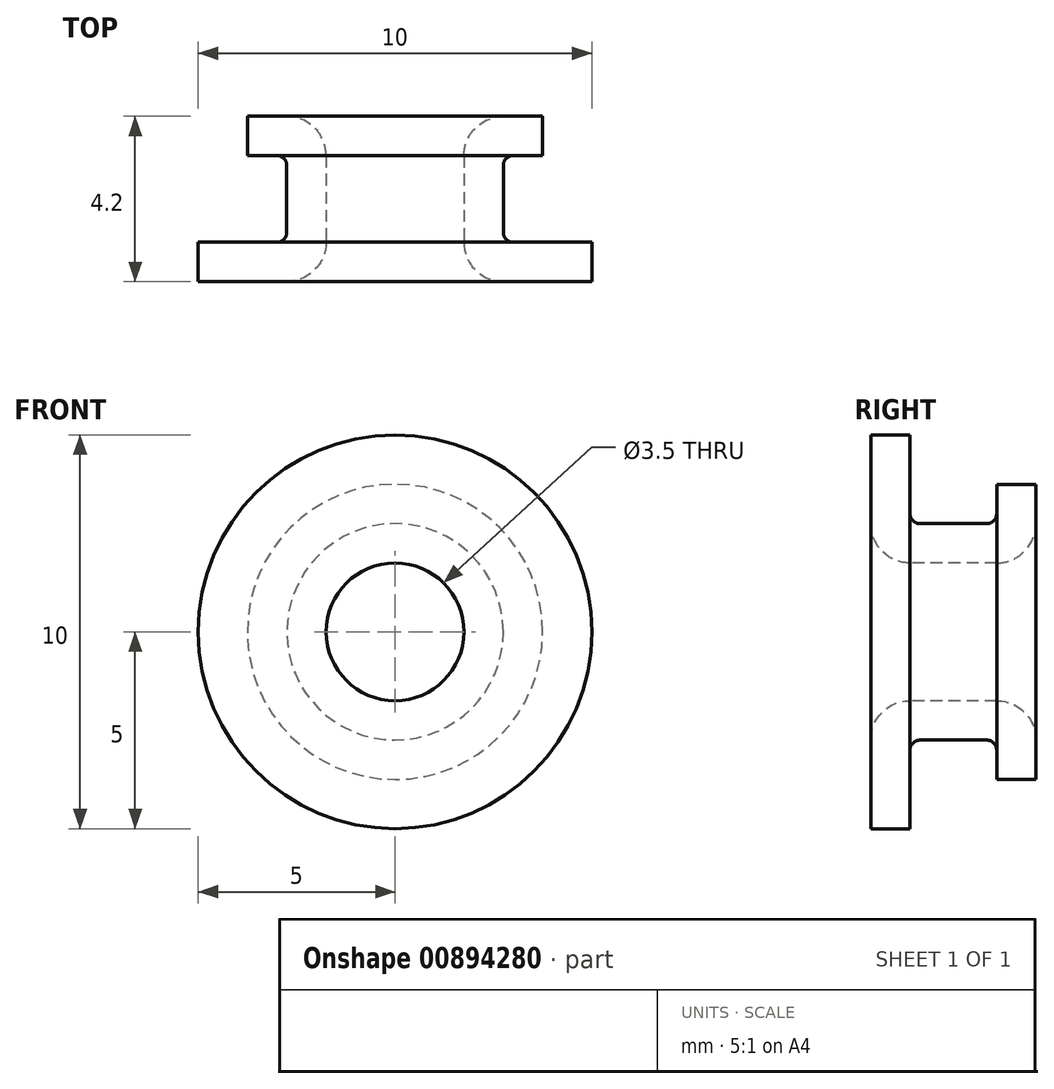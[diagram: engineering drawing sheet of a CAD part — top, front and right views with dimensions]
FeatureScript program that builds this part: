
annotation { "Feature Type Name" : "Feature", "Feature Type Description" : "" }
export const myFeature = defineFeature(function(context is Context, id is Id, definition is map)
    precondition{}
    {
        {
            var Q0;
            Q0=qCreatedBy(makeId("Right.planeOp"),FACE);
            var sketch = newSketch(context, id + "F0", { "sketchPlane" : qUnion([Q0])});
            skLineSegment(sketch, "E0", {"start": v(1, 5) * mm, "end": v(1, 3) * mm});
            skLineSegment(sketch, "E1", {"start": v(1.25, 2.75) * mm, "end": v(2.95, 2.75) * mm});
            skLineSegment(sketch, "E2", {"start": v(1, 1.75) * mm, "end": v(3.2, 1.75) * mm});
            skLineSegment(sketch, "E3", {"start": v(0, 0) * mm, "end": v(4.2, 0) * mm});
            skPoint(sketch, "E4.visualSharp", {"position": v(1, 2.75) * mm});
            skArc(sketch, "E4.filletArc", {"start": v(1, 3) * mm, "mid": v(1.07, 2.82) * mm, "end": v(1.25, 2.75) * mm});
            skPoint(sketch, "E5.visualSharp", {"position": v(3.2, 2.75) * mm});
            skLineSegment(sketch, "E6", {"start": v(4.2, 3.75) * mm, "end": v(4.2, 2.75) * mm});
            skArc(sketch, "E7", {"start": v(0, 2.75) * mm, "mid": v(0.3, 2.04) * mm, "end": v(1, 1.75) * mm});
            skLineSegment(sketch, "E8", {"start": v(0, 2.75) * mm, "end": v(0, 5) * mm});
            skLineSegment(sketch, "E9", {"start": v(1, 5) * mm, "end": v(0, 5) * mm});
            skLineSegment(sketch, "E10", {"start": v(4.2, 3.75) * mm, "end": v(3.2, 3.75) * mm});
            skLineSegment(sketch, "E11", {"start": v(3.2, 3.75) * mm, "end": v(3.2, 3) * mm});
            skArc(sketch, "E12.filletArc", {"start": v(2.95, 2.75) * mm, "mid": v(3.13, 2.82) * mm, "end": v(3.2, 3) * mm});
            skArc(sketch, "E13.filletArc", {"start": v(3.2, 1.75) * mm, "mid": v(3.9, 2.04) * mm, "end": v(4.2, 2.75) * mm});
            skSolve(sketch);
        }
        {
            var Q0;
            Q0=makeQuery(id+"F0.imprint","IMPRINT",FACE,{"disambiguationData":[TD([[makeQuery(id+"F0.imprint","IMPRINT",EDGE,{"derivedFrom":sQuery(id+"F0.wireOp",EDGE,"E0")}),-1.0]])]});
            var Q1;
            Q1=sQuery(id+"F0.wireOp",EDGE,"E3");
            revolve(context, id + "F1", {"surfaceOperationType" : NewSurfaceOperationType.NEW, "entities" : qUnion([Q0]), "axis" : qUnion([Q1]), "revolveType" : RevolveType.FULL});
        }
    });
